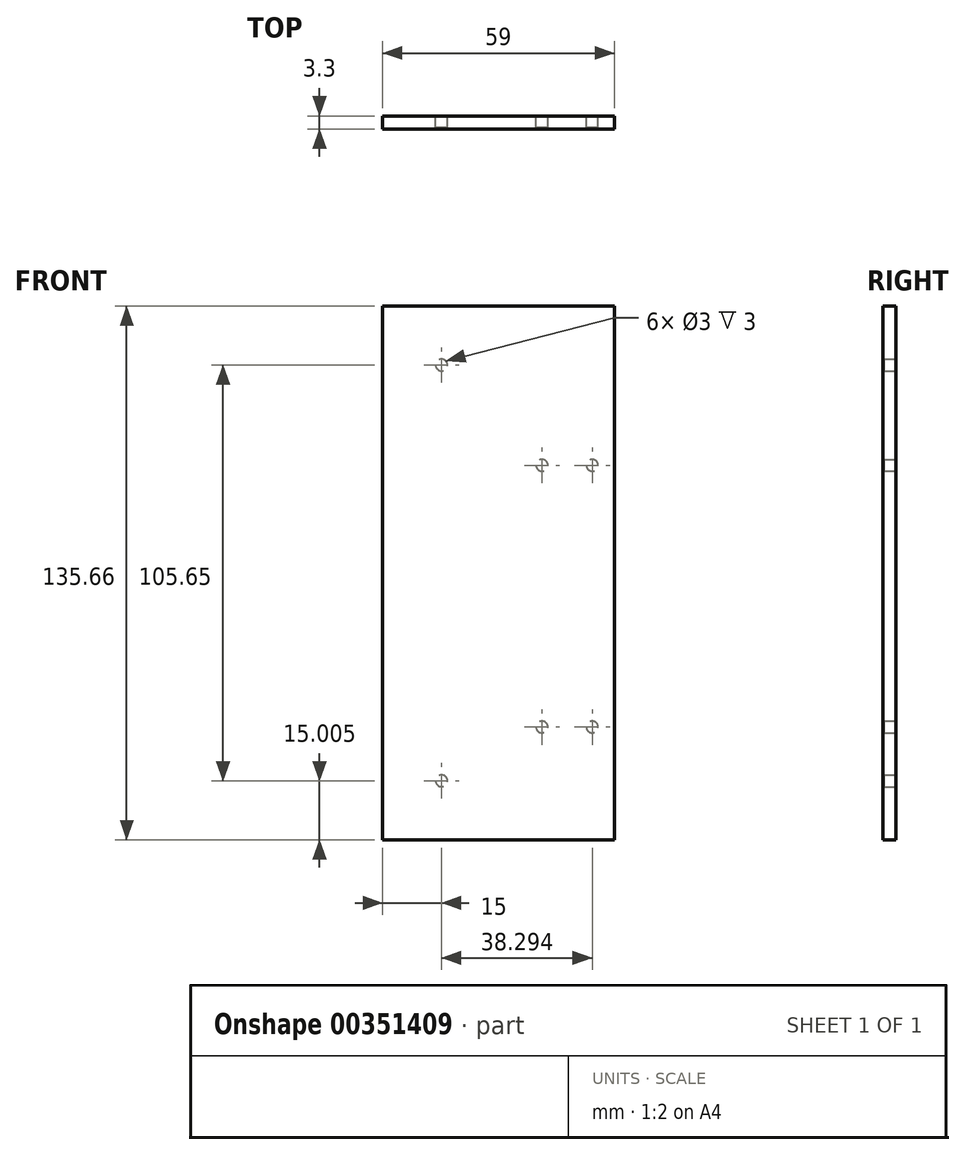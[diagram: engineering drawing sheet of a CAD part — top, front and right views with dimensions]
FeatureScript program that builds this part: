
annotation { "Feature Type Name" : "Feature", "Feature Type Description" : "" }
export const myFeature = defineFeature(function(context is Context, id is Id, definition is map)
    precondition{}
    {
        {
            var Q0;
            Q0=qCreatedBy(makeId("Front.planeOp"),FACE);
            var sketch = newSketch(context, id + "F0", { "sketchPlane" : qUnion([Q0])});
            skLineSegment(sketch, "E0.bottom", {"start": v(29.5, 67.83) * mm, "end": v(-29.5, 67.83) * mm});
            skLineSegment(sketch, "E0.top", {"start": v(29.5, -67.83) * mm, "end": v(-29.5, -67.83) * mm});
            skLineSegment(sketch, "E0.left", {"start": v(29.5, 67.83) * mm, "end": v(29.5, -67.83) * mm});
            skLineSegment(sketch, "E0.right", {"start": v(-29.5, 67.83) * mm, "end": v(-29.5, -67.83) * mm});
            skPoint(sketch, "E0.middle", {"position": v(0, 0) * mm});
            skSolve(sketch);
        }
        {
            var Q0;
            Q0 = qSketchRegion(id + "F0", true);
            extrude(context, id + "F1", {"entities" : qUnion([Q0]), "depth" : 3.3 * mm});
        }
        {
            var Q0;
            Q0=makeQuery(id+"F1.opExtrude","CAP_FACE",FACE,{"disambiguationData":[OSD([sQuery(id+"F0.wireOp",EDGE,"E0.bottom"),sQuery(id+"F0.wireOp",EDGE,"E0.top"),sQuery(id+"F0.wireOp",EDGE,"E0.left"),sQuery(id+"F0.wireOp",EDGE,"E0.right")])],"isStart":true});
            var sketch = newSketch(context, id + "F2", { "sketchPlane" : qUnion([Q0])});
            skCircle(sketch, "E1", {"center": v(14.5, 52.83) * mm, "radius": 1.5 * mm});
            skCircle(sketch, "E2", {"center": v(14.5, -52.83) * mm, "radius": 1.5 * mm});
            skSolve(sketch);
        }
        {
            var Q0;
            Q0 = qSketchRegion(id + "F2", true);
            extrude(context, id + "F3", {"entities" : qUnion([Q0]), "operationType" : NewBodyOperationType.REMOVE, "oppositeDirection" : true, "depth" : 3 * mm});
        }
        {
            var Q0;
            Q0=makeQuery(id+"F1.opExtrude","CAP_FACE",FACE,{"disambiguationData":[OSD([sQuery(id+"F0.wireOp",EDGE,"E0.bottom"),sQuery(id+"F0.wireOp",EDGE,"E0.top"),sQuery(id+"F0.wireOp",EDGE,"E0.left"),sQuery(id+"F0.wireOp",EDGE,"E0.right")])],"isStart":true});
            var sketch = newSketch(context, id + "F4", { "sketchPlane" : qUnion([Q0])});
            skLineSegment(sketch, "E3", {"start": v(-23.8, 67.83) * mm, "end": v(-23.8, -67.83) * mm, "construction": true});
            skLineSegment(sketch, "E4", {"start": v(-11.02, 67.83) * mm, "end": v(-11.02, -67.83) * mm, "construction": true});
            skCircle(sketch, "E5", {"center": v(-23.8, 27.36) * mm, "radius": 1.5 * mm});
            skCircle(sketch, "E6", {"center": v(-11.02, 27.36) * mm, "radius": 1.5 * mm});
            skCircle(sketch, "E7", {"center": v(-23.8, -39.14) * mm, "radius": 1.5 * mm});
            skCircle(sketch, "E8", {"center": v(-11.02, -39.14) * mm, "radius": 1.5 * mm});
            skSolve(sketch);
        }
        {
            var Q0;
            Q0 = qSketchRegion(id + "F4", true);
            extrude(context, id + "F5", {"entities" : qUnion([Q0]), "operationType" : NewBodyOperationType.REMOVE, "oppositeDirection" : true, "depth" : 3 * mm});
        }
    });
